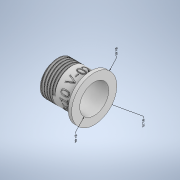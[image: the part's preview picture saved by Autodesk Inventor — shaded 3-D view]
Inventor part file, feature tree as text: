
AUTODESK INVENTOR PART (.ipt)
format: ipt  version: 2021.1 (Build 251245010, 245A)  size: 875,520 bytes
history: native  units: in
note: dims shown in document units (in); Inventor stores cm internally (conversion verified against a paired STEP export)
features: other x4, sketch x3, revolve x1, plane x1, emboss x1, helix x1
ambient origin geometry x8: Origin, YZ Plane, XZ Plane, XY Plane, X Axis, Y Axis, Z Axis, Center Point
bodies: Solid1 (feature_tree)
feature tree (11):
  other  "Annotations"
  revolve  "Revolution1"  [1 undecoded]
  plane  "Work Plane1"
  emboss  "Emboss1"
  helix  "Coil1"  [1 undecoded]
  sketch  "Sketch2"  dims[d0=0.825in d1=0.53in d2=0.125in]
  sketch  "Sketch4"  dims[d3=1.0in]
  sketch  "Sketch5"  dims[d4=90.0deg d5=0.625in d6=0.25in d10=60.0deg d11=0.0121in d12=60.0deg d13=60.0deg d15=0.1in d16=0.2in d17=0.05in d18=0.625in d19=0.5655in d20=30.0deg d21=0.1in d22=0.625in d23=0.3937in d24=0.0in d25=90.0deg d26=90.0deg d27=0.0in d28=0.0in d35=0.35in d36=0.05in d37=0.0in d38=0.095in d29=2.0173in d30=1.65in d31=2.2078in d32=1.25in d33=1.04in d34=1.06in]
  other  "Diameter Dimension 1"
  other  "Diameter Dimension 2"
  other  "Diameter Dimension 3"
note: 2 required parameter values undecoded (feature->parameter linkage not recoverable at this tier; creation-order binding heuristic only, values carry confidence <= 0.55)